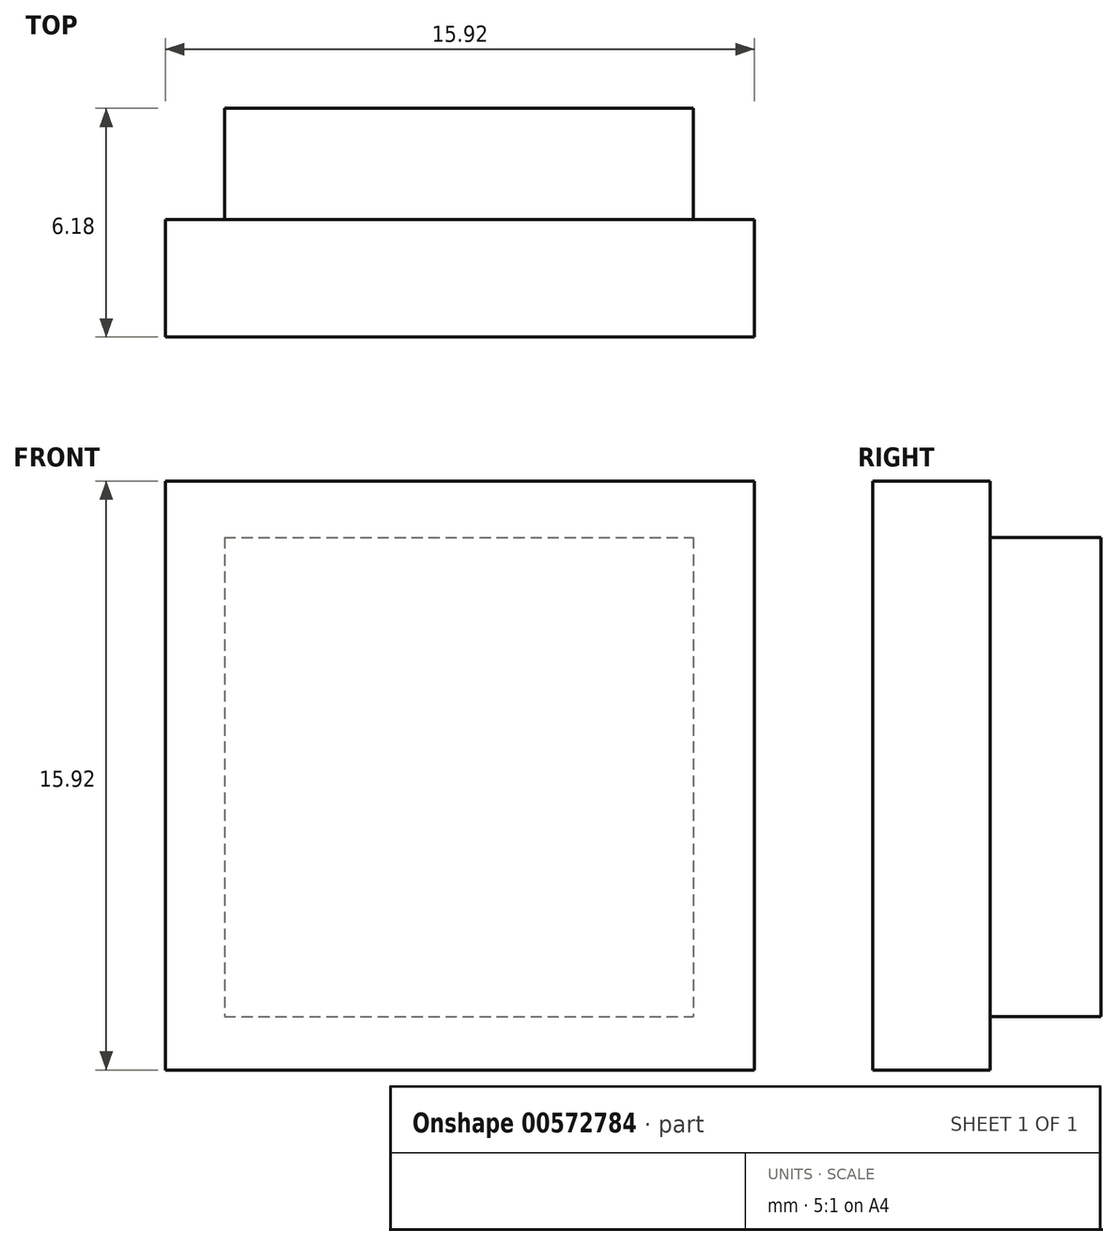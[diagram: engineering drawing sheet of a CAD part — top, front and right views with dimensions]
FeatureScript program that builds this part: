
annotation { "Feature Type Name" : "Feature", "Feature Type Description" : "" }
export const myFeature = defineFeature(function(context is Context, id is Id, definition is map)
    precondition{}
    {
        {
            var Q0;
            Q0=qCreatedBy(makeId("Front.planeOp"),FACE);
            var sketch = newSketch(context, id + "F0", { "sketchPlane" : qUnion([Q0])});
            skLineSegment(sketch, "E0.bottom", {"start": v(-3.9, 5.88) * mm, "end": v(12.02, 5.88) * mm});
            skLineSegment(sketch, "E0.top", {"start": v(-3.9, -10.04) * mm, "end": v(12.02, -10.04) * mm});
            skLineSegment(sketch, "E0.left", {"start": v(-3.9, 5.88) * mm, "end": v(-3.9, -10.04) * mm});
            skLineSegment(sketch, "E0.right", {"start": v(12.02, 5.88) * mm, "end": v(12.02, -10.04) * mm});
            skSolve(sketch);
        }
        {
            var Q0;
            Q0=makeQuery(id+"F0.imprint","IMPRINT",FACE,{"disambiguationData":[TD([[makeQuery(id+"F0.imprint","IMPRINT",EDGE,{"derivedFrom":sQuery(id+"F0.wireOp",EDGE,"E0.bottom")}),-1.0]])]});
            extrude(context, id + "F1", {"entities" : qUnion([Q0]), "oppositeDirection" : true, "depth" : 3.18 * mm, "offsetDistance" : 25 * mm});
        }
        {
            var Q0;
            Q0=makeQuery(id+"F1.opExtrude","CAP_FACE",FACE,{"disambiguationData":[OSD([sQuery(id+"F0.wireOp",EDGE,"E0.bottom"),sQuery(id+"F0.wireOp",EDGE,"E0.top"),sQuery(id+"F0.wireOp",EDGE,"E0.left"),sQuery(id+"F0.wireOp",EDGE,"E0.right")])],"isStart":true});
            var sketch = newSketch(context, id + "F2", { "sketchPlane" : qUnion([Q0])});
            skLineSegment(sketch, "E1.bottom", {"start": v(-2.3, 4.36) * mm, "end": v(10.37, 4.36) * mm});
            skLineSegment(sketch, "E1.top", {"start": v(-2.3, -8.6) * mm, "end": v(10.37, -8.6) * mm});
            skLineSegment(sketch, "E1.left", {"start": v(-2.3, 4.36) * mm, "end": v(-2.3, -8.6) * mm});
            skLineSegment(sketch, "E1.right", {"start": v(10.37, 4.36) * mm, "end": v(10.37, -8.6) * mm});
            skSolve(sketch);
        }
        {
            var Q0;
            Q0=makeQuery(id+"F2.imprint","IMPRINT",FACE,{"disambiguationData":[TD([[makeQuery(id+"F2.imprint","IMPRINT",EDGE,{"derivedFrom":sQuery(id+"F2.wireOp",EDGE,"E1.bottom")}),-1.0]])]});
            extrude(context, id + "F3", {"entities" : qUnion([Q0]), "operationType" : NewBodyOperationType.ADD, "oppositeDirection" : true, "depth" : 6.18 * mm, "offsetDistance" : 25 * mm});
        }
    });
